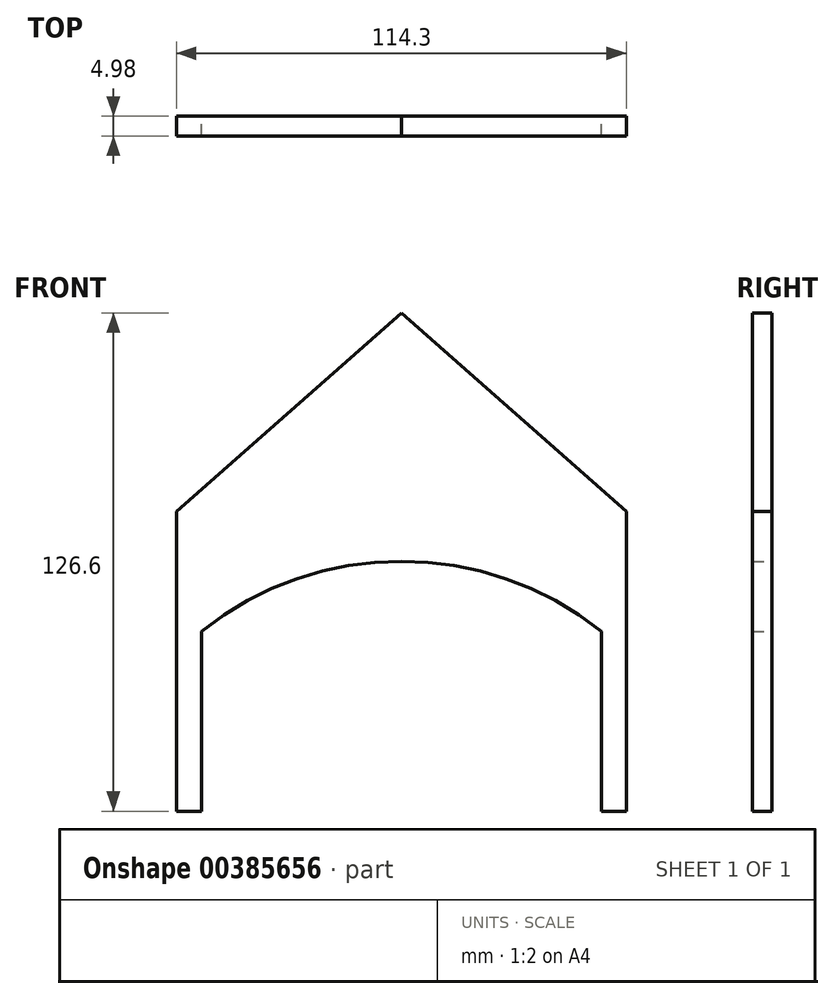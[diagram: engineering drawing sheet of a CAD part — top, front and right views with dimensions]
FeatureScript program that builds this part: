
annotation { "Feature Type Name" : "Feature", "Feature Type Description" : "" }
export const myFeature = defineFeature(function(context is Context, id is Id, definition is map)
    precondition{}
    {
        {
            var Q0;
            Q0=qCreatedBy(makeId("Front.planeOp"),FACE);
            var sketch = newSketch(context, id + "F0", { "sketchPlane" : qUnion([Q0])});
            skLineSegment(sketch, "E0.bottom", {"start": v(57.15, 38.1) * mm, "end": v(-57.15, 38.1) * mm});
            skLineSegment(sketch, "E0.top", {"start": v(57.15, -38.1) * mm, "end": v(50.8, -38.1) * mm});
            skLineSegment(sketch, "E0.left", {"start": v(57.15, 38.1) * mm, "end": v(57.15, -38.1) * mm});
            skLineSegment(sketch, "E0.right", {"start": v(-57.15, 38.1) * mm, "end": v(-57.15, -38.1) * mm});
            skPoint(sketch, "E0.middle", {"position": v(0, 0) * mm});
            skLineSegment(sketch, "E1", {"start": v(-50.8, -38.1) * mm, "end": v(-50.8, 25.4) * mm});
            skLineSegment(sketch, "E2", {"start": v(-50.8, 25.4) * mm, "end": v(50.8, 25.4) * mm});
            skLineSegment(sketch, "E3", {"start": v(50.8, 25.4) * mm, "end": v(50.8, -38.1) * mm});
            skLineSegment(sketch, "E4.trimOffspring", {"start": v(-50.8, -38.1) * mm, "end": v(-57.15, -38.1) * mm});
            skLineSegment(sketch, "E5", {"start": v(-57.15, 38.1) * mm, "end": v(0, 88.5) * mm});
            skLineSegment(sketch, "E6", {"start": v(0, 88.5) * mm, "end": v(57.15, 38.1) * mm});
            skArc(sketch, "E7", {"start": v(50.8, 7.62) * mm, "mid": v(0, 25.4) * mm, "end": v(-50.8, 7.62) * mm});
            skSolve(sketch);
        }
        {
            var Q0;
            Q0=qSketchRegion(id+"F0",true);
            extrude(context, id + "F1", {"entities" : qUnion([Q0]), "depth" : 4.98 * mm});
        }
    });
